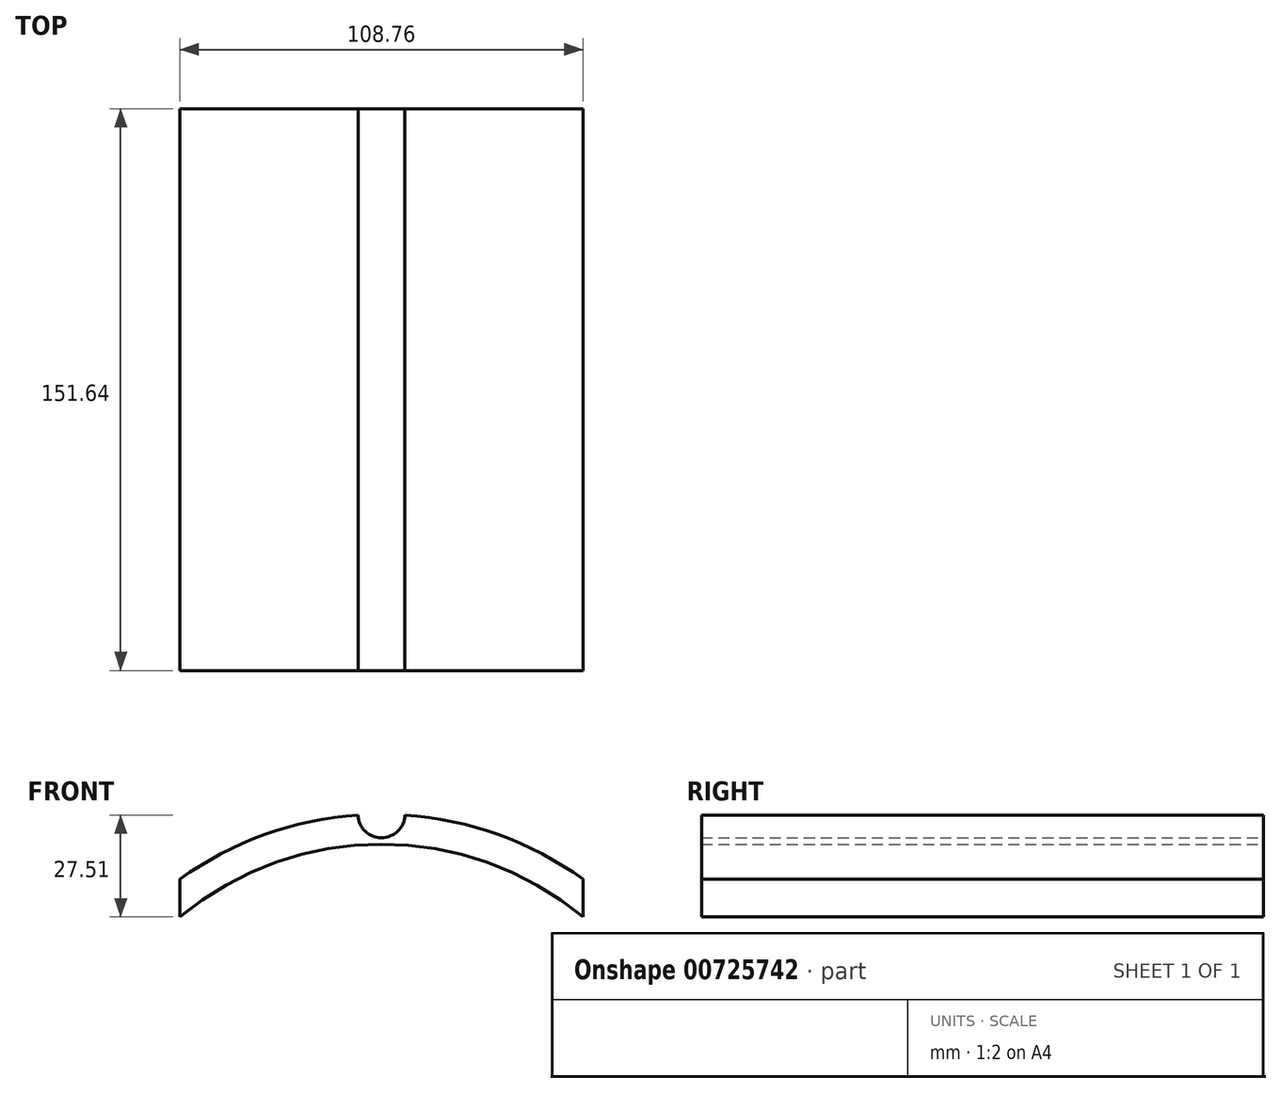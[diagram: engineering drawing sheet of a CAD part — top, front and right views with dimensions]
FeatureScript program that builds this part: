
annotation { "Feature Type Name" : "Feature", "Feature Type Description" : "" }
export const myFeature = defineFeature(function(context is Context, id is Id, definition is map)
    precondition{}
    {
        {
            var Q0;
            Q0=qCreatedBy(makeId("Front.planeOp"),FACE);
            var sketch = newSketch(context, id + "F0", { "sketchPlane" : qUnion([Q0])});
            skCircle(sketch, "E0", {"center": v(0, 0) * mm, "radius": 85.03 * mm});
            skCircle(sketch, "E1", {"center": v(0, 0) * mm, "radius": 100.65 * mm});
            skLineSegment(sketch, "E2", {"start": v(0, 0) * mm, "end": v(64.7, 77.1) * mm});
            skLineSegment(sketch, "E3", {"start": v(0, 0) * mm, "end": v(-64.7, 77.1) * mm});
            skPoint(sketch, "E4", {"position": v(-54.65, 65.13) * mm});
            skPoint(sketch, "E5", {"position": v(54.65, 65.13) * mm});
            skLineSegment(sketch, "E6", {"start": v(-54.65, 65.13) * mm, "end": v(-54.65, 84.52) * mm});
            skLineSegment(sketch, "E7", {"start": v(54.65, 65.13) * mm, "end": v(54.65, 84.52) * mm});
            skLineSegment(sketch, "E8", {"start": v(-54.38, 65.36) * mm, "end": v(-54.38, 84.7) * mm});
            skLineSegment(sketch, "E9", {"start": v(54.38, 65.36) * mm, "end": v(54.38, 84.7) * mm});
            skLineSegment(sketch, "E10", {"start": v(0, 85.03) * mm, "end": v(0, 100.65) * mm});
            skSolve(sketch);
        }
        {
            var Q0;
            {var subQ0=sQuery(id+"F0.wireOp",EDGE,"E8");Q0=makeQuery(id+"F0.imprint","IMPRINT",FACE,{"disambiguationData":[TD([[makeQuery(id+"F0.imprint","IMPRINT",EDGE,{"derivedFrom":subQ0}),-1.0]])]});}
            var Q1;
            {var subQ0=sQuery(id+"F0.wireOp",EDGE,"E9");Q1=makeQuery(id+"F0.imprint","IMPRINT",FACE,{"disambiguationData":[TD([[makeQuery(id+"F0.imprint","IMPRINT",EDGE,{"derivedFrom":subQ0}),1.0]])]});}
            extrude(context, id + "F1", {"entities" : qUnion([Q0, Q1]), "depth" : 151.64 * mm, "offsetDistance" : 25.4 * mm});
        }
        {
            var Q0;
            Q0=makeQuery(id+"F1.opExtrude","CAP_FACE",FACE,{"disambiguationData":[OSD([sQuery(id+"F0.wireOp",EDGE,"E0"),sQuery(id+"F0.wireOp",EDGE,"E1"),sQuery(id+"F0.wireOp",EDGE,"E2"),sQuery(id+"F0.wireOp",EDGE,"E3")])],"isStart":true});
            var sketch = newSketch(context, id + "F2", { "sketchPlane" : qUnion([Q0])});
            skLineSegment(sketch, "E11", {"start": v(0, 0) * mm, "end": v(0, 100.65) * mm});
            skLineSegment(sketch, "E12", {"start": v(0, 0) * mm, "end": v(42.54, 91.22) * mm});
            skLineSegment(sketch, "E13", {"start": v(0, 0) * mm, "end": v(-42.54, 91.22) * mm});
            skCircle(sketch, "E14", {"center": v(0, 0) * mm, "radius": 100.65 * mm});
            skCircle(sketch, "E15", {"center": v(0, 0) * mm, "radius": 93.1 * mm});
            skCircle(sketch, "E16", {"center": v(0, 0) * mm, "radius": 85.03 * mm});
            skPoint(sketch, "E17", {"position": v(0, 93.1) * mm});
            skPoint(sketch, "E18", {"position": v(-39.34, 84.37) * mm});
            skPoint(sketch, "E19", {"position": v(39.34, 84.37) * mm});
            skCircle(sketch, "E20", {"center": v(-39.34, 84.37) * mm, "radius": 6.35 * mm});
            skCircle(sketch, "E21", {"center": v(0, 93.1) * mm, "radius": 6.35 * mm});
            skCircle(sketch, "E22", {"center": v(39.34, 84.37) * mm, "radius": 6.35 * mm});
            skSolve(sketch);
        }
        {
            var Q0;
            {var subQ0=sQuery(id+"F2.wireOp",EDGE,"E15");var subQ1=sQuery(id+"F2.wireOp",EDGE,"E13");var subQ2=makeQuery(id+"F2.imprint","INTERSECT",VERTEX,{"derivedFrom":[subQ1,subQ0]});Q0=makeQuery(id+"F2.imprint","IMPRINT",FACE,{"disambiguationData":[TD([[makeQuery(id+"F2.imprint","IMPRINT",EDGE,{"disambiguationData":[TD([[subQ2,-1.0]])],"derivedFrom":subQ1}),-1.0]])]});}
            var Q1;
            {var subQ0=sQuery(id+"F2.wireOp",EDGE,"E15");var subQ1=sQuery(id+"F2.wireOp",EDGE,"E13");var subQ2=makeQuery(id+"F2.imprint","INTERSECT",VERTEX,{"derivedFrom":[subQ1,subQ0]});Q1=makeQuery(id+"F2.imprint","IMPRINT",FACE,{"disambiguationData":[TD([[makeQuery(id+"F2.imprint","IMPRINT",EDGE,{"disambiguationData":[TD([[subQ2,-1.0]])],"derivedFrom":subQ1}),1.0]])]});}
            var Q2;
            {var subQ0=sQuery(id+"F2.wireOp",EDGE,"E20");var subQ1=sQuery(id+"F2.wireOp",EDGE,"E13");var subQ2=makeQuery(id+"F2.imprint","INTERSECT",VERTEX,{"disambiguationData":[OD(0.0)],"derivedFrom":[subQ1,subQ0]});Q2=makeQuery(id+"F2.imprint","IMPRINT",FACE,{"disambiguationData":[TD([[makeQuery(id+"F2.imprint","IMPRINT",EDGE,{"disambiguationData":[TD([[subQ2,-1.0]])],"derivedFrom":subQ1}),1.0]])]});}
            var Q3;
            {var subQ0=sQuery(id+"F2.wireOp",EDGE,"E20");var subQ1=sQuery(id+"F2.wireOp",EDGE,"E13");var subQ2=makeQuery(id+"F2.imprint","INTERSECT",VERTEX,{"disambiguationData":[OD(0.0)],"derivedFrom":[subQ1,subQ0]});Q3=makeQuery(id+"F2.imprint","IMPRINT",FACE,{"disambiguationData":[TD([[makeQuery(id+"F2.imprint","IMPRINT",EDGE,{"disambiguationData":[TD([[subQ2,-1.0]])],"derivedFrom":subQ1}),-1.0]])]});}
            var Q4;
            {var subQ0=sQuery(id+"F2.wireOp",EDGE,"E15");var subQ1=sQuery(id+"F2.wireOp",EDGE,"E11");var subQ2=makeQuery(id+"F2.imprint","INTERSECT",VERTEX,{"derivedFrom":[subQ1,subQ0]});Q4=makeQuery(id+"F2.imprint","IMPRINT",FACE,{"disambiguationData":[TD([[makeQuery(id+"F2.imprint","IMPRINT",EDGE,{"disambiguationData":[TD([[subQ2,-1.0]])],"derivedFrom":subQ1}),1.0]])]});}
            var Q5;
            {var subQ0=sQuery(id+"F2.wireOp",EDGE,"E15");var subQ1=sQuery(id+"F2.wireOp",EDGE,"E11");var subQ2=makeQuery(id+"F2.imprint","INTERSECT",VERTEX,{"derivedFrom":[subQ1,subQ0]});Q5=makeQuery(id+"F2.imprint","IMPRINT",FACE,{"disambiguationData":[TD([[makeQuery(id+"F2.imprint","IMPRINT",EDGE,{"disambiguationData":[TD([[subQ2,-1.0]])],"derivedFrom":subQ1}),-1.0]])]});}
            var Q6;
            {var subQ0=sQuery(id+"F2.wireOp",EDGE,"E21");var subQ1=sQuery(id+"F2.wireOp",EDGE,"E11");var subQ2=makeQuery(id+"F2.imprint","INTERSECT",VERTEX,{"disambiguationData":[OD(0.0)],"derivedFrom":[subQ1,subQ0]});Q6=makeQuery(id+"F2.imprint","IMPRINT",FACE,{"disambiguationData":[TD([[makeQuery(id+"F2.imprint","IMPRINT",EDGE,{"disambiguationData":[TD([[subQ2,-1.0]])],"derivedFrom":subQ1}),-1.0]])]});}
            var Q7;
            {var subQ0=sQuery(id+"F2.wireOp",EDGE,"E21");var subQ1=sQuery(id+"F2.wireOp",EDGE,"E11");var subQ2=makeQuery(id+"F2.imprint","INTERSECT",VERTEX,{"disambiguationData":[OD(0.0)],"derivedFrom":[subQ1,subQ0]});Q7=makeQuery(id+"F2.imprint","IMPRINT",FACE,{"disambiguationData":[TD([[makeQuery(id+"F2.imprint","IMPRINT",EDGE,{"disambiguationData":[TD([[subQ2,-1.0]])],"derivedFrom":subQ1}),1.0]])]});}
            var Q8;
            {var subQ0=sQuery(id+"F2.wireOp",EDGE,"E15");var subQ1=sQuery(id+"F2.wireOp",EDGE,"E12");var subQ2=makeQuery(id+"F2.imprint","INTERSECT",VERTEX,{"derivedFrom":[subQ1,subQ0]});Q8=makeQuery(id+"F2.imprint","IMPRINT",FACE,{"disambiguationData":[TD([[makeQuery(id+"F2.imprint","IMPRINT",EDGE,{"disambiguationData":[TD([[subQ2,-1.0]])],"derivedFrom":subQ1}),1.0]])]});}
            var Q9;
            {var subQ0=sQuery(id+"F2.wireOp",EDGE,"E15");var subQ1=sQuery(id+"F2.wireOp",EDGE,"E12");var subQ2=makeQuery(id+"F2.imprint","INTERSECT",VERTEX,{"derivedFrom":[subQ1,subQ0]});Q9=makeQuery(id+"F2.imprint","IMPRINT",FACE,{"disambiguationData":[TD([[makeQuery(id+"F2.imprint","IMPRINT",EDGE,{"disambiguationData":[TD([[subQ2,-1.0]])],"derivedFrom":subQ1}),-1.0]])]});}
            var Q10;
            {var subQ0=sQuery(id+"F2.wireOp",EDGE,"E22");var subQ1=sQuery(id+"F2.wireOp",EDGE,"E12");var subQ2=makeQuery(id+"F2.imprint","INTERSECT",VERTEX,{"disambiguationData":[OD(0.0)],"derivedFrom":[subQ1,subQ0]});Q10=makeQuery(id+"F2.imprint","IMPRINT",FACE,{"disambiguationData":[TD([[makeQuery(id+"F2.imprint","IMPRINT",EDGE,{"disambiguationData":[TD([[subQ2,-1.0]])],"derivedFrom":subQ1}),-1.0]])]});}
            var Q11;
            {var subQ0=sQuery(id+"F2.wireOp",EDGE,"E22");var subQ1=sQuery(id+"F2.wireOp",EDGE,"E12");var subQ2=makeQuery(id+"F2.imprint","INTERSECT",VERTEX,{"disambiguationData":[OD(0.0)],"derivedFrom":[subQ1,subQ0]});Q11=makeQuery(id+"F2.imprint","IMPRINT",FACE,{"disambiguationData":[TD([[makeQuery(id+"F2.imprint","IMPRINT",EDGE,{"disambiguationData":[TD([[subQ2,-1.0]])],"derivedFrom":subQ1}),1.0]])]});}
            extrude(context, id + "F3", {"entities" : qUnion([Q0, Q1, Q2, Q3, Q4, Q5, Q6, Q7, Q8, Q9, Q10, Q11]), "operationType" : NewBodyOperationType.REMOVE, "endBound" : BoundingType.THROUGH_ALL, "oppositeDirection" : true, "depth" : 25.4 * mm, "offsetDistance" : 25.4 * mm});
        }
    });
